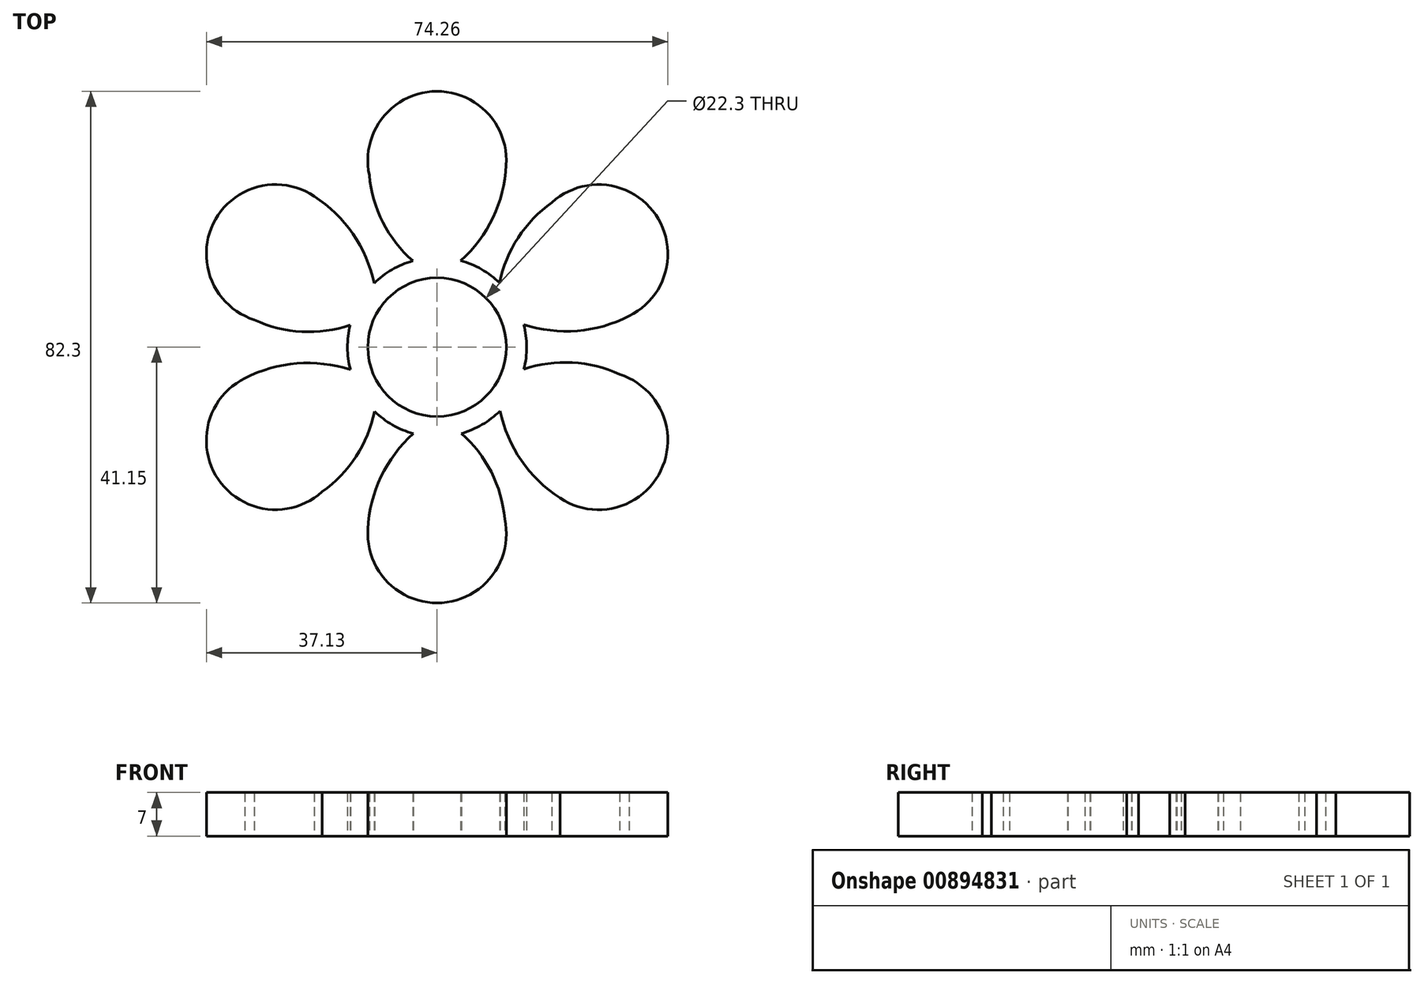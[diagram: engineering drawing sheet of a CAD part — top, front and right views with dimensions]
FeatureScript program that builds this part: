
annotation { "Feature Type Name" : "Feature", "Feature Type Description" : "" }
export const myFeature = defineFeature(function(context is Context, id is Id, definition is map)
    precondition{}
    {
        {
            var Q0;
            Q0=qCreatedBy(makeId("Top.planeOp"),FACE);
            var sketch = newSketch(context, id + "F0", { "sketchPlane" : qUnion([Q0])});
            skCircle(sketch, "E0", {"center": v(0, 0) * mm, "radius": 11.15 * mm});
            skCircle(sketch, "E1", {"center": v(0, 30) * mm, "radius": 11.15 * mm});
            skLineSegment(sketch, "E2", {"start": v(0, 30) * mm, "end": v(0, 0) * mm, "construction": true});
            skCircle(sketch, "E3.1.0", {"center": v(-25.98, 15) * mm, "radius": 11.15 * mm});
            skCircle(sketch, "E3.2.0", {"center": v(-25.98, -15) * mm, "radius": 11.15 * mm});
            skCircle(sketch, "E3.3.0", {"center": v(0, -30) * mm, "radius": 11.15 * mm});
            skCircle(sketch, "E3.4.0", {"center": v(25.98, -15) * mm, "radius": 11.15 * mm});
            skCircle(sketch, "E3.5.0", {"center": v(25.98, 15) * mm, "radius": 11.15 * mm});
            skArc(sketch, "E4", {"start": v(0, 11.15) * mm, "mid": v(8.07, 19.1) * mm, "end": v(11.15, 30) * mm});
            skArc(sketch, "E5", {"start": v(-10.97, 30.36) * mm, "mid": v(-8.23, 19.19) * mm, "end": v(0, 11.15) * mm});
            skArc(sketch, "E6.1.0", {"start": v(-9.66, 5.58) * mm, "mid": v(-12.5, 16.54) * mm, "end": v(-20.4, 24.66) * mm});
            skArc(sketch, "E6.1.1", {"start": v(-31.78, 5.68) * mm, "mid": v(-20.73, 2.46) * mm, "end": v(-9.66, 5.58) * mm});
            skArc(sketch, "E6.2.0", {"start": v(-9.66, -5.57) * mm, "mid": v(-20.58, -2.56) * mm, "end": v(-31.56, -5.34) * mm});
            skArc(sketch, "E6.2.1", {"start": v(-20.8, -24.68) * mm, "mid": v(-12.5, -16.72) * mm, "end": v(-9.66, -5.58) * mm});
            skArc(sketch, "E6.3.0", {"start": v(0, -11.15) * mm, "mid": v(-8.07, -19.1) * mm, "end": v(-11.15, -30) * mm});
            skArc(sketch, "E6.3.1", {"start": v(10.97, -30.36) * mm, "mid": v(8.23, -19.19) * mm, "end": v(0, -11.15) * mm});
            skArc(sketch, "E6.4.0", {"start": v(9.66, -5.58) * mm, "mid": v(12.5, -16.54) * mm, "end": v(20.4, -24.66) * mm});
            skArc(sketch, "E6.4.1", {"start": v(31.78, -5.68) * mm, "mid": v(20.73, -2.46) * mm, "end": v(9.66, -5.58) * mm});
            skArc(sketch, "E6.5.0", {"start": v(9.66, 5.57) * mm, "mid": v(20.58, 2.56) * mm, "end": v(31.56, 5.34) * mm});
            skArc(sketch, "E6.5.1", {"start": v(20.8, 24.68) * mm, "mid": v(12.5, 16.72) * mm, "end": v(9.66, 5.58) * mm});
            skCircle(sketch, "E7", {"center": v(0, 0) * mm, "radius": 14.42 * mm});
            skSolve(sketch);
        }
        {
            var Q0;
            Q0 = qSketchRegion(id + "F0", true);
            extrude(context, id + "F1", {"entities" : qUnion([Q0]), "depth" : 7 * mm, "offsetDistance" : 25 * mm});
        }
    });
